# Revit family: Скамейка стальная полукруглая «Авиньон» Арт 15497
name_source: partatom
category: Антураж
revit_build: Autodesk Revit 2018 (Build: 20180423_1000(x64)
units: mm (PartAtom-declared; Revit-internal decimal feet)

## family parameters
Всегда вертикально = Да
Источник визуального образа = Геометрия семейства
На основе рабочей плоскости = Нет
Общий = Нет
При загрузке вырезать с полостями = Нет
Точка расчета площади = Нет

## types (2) — shared parameters
URL = https://hobbyka.ru
Артикул товара = Арт. 15497
Высота = 1000 мм
Группа модели = Скамейки
Изготовитель = ООО «Хоббика»
Изображение типоразмера = Скамейка стальная полукруглая «Авиньон» Арт 15497.jpg
Материал изделия = Сталь, дерево
Цвет лавки = Дерево
Цвет опоры = Сталь
Ширина = 740 мм

## per-type parameters (varying)
| type | Версия 1,56 м | Версия 2,92 м | Длина | Описание |
| Версия 1,56 м | Да | Нет | 1560 мм | Скамейка стальная полукруглая «Авиньон». Версия 1,56 м |
| Версия 2,92 м | Нет | Да | 2920 мм | Скамейка стальная полукруглая «Авиньон». Версия 2,92 м |
